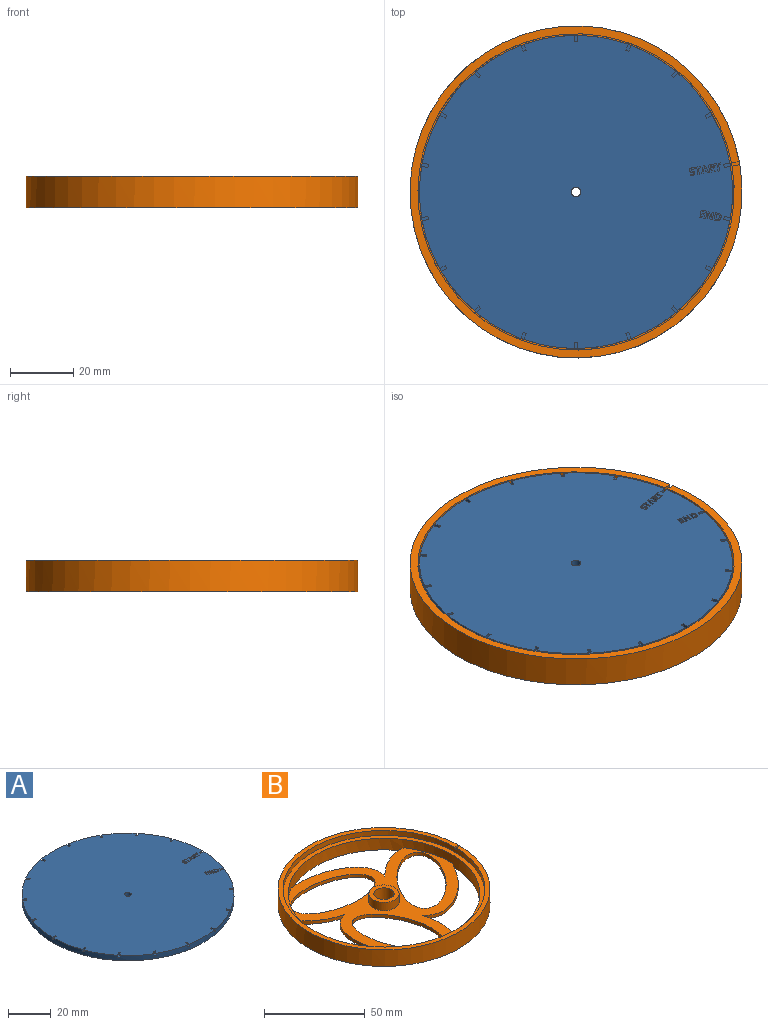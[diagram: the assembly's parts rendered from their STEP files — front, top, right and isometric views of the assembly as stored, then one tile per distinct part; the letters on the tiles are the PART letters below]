
ASSEMBLY  parts=2 mates=1
PART A: 206 faces, bbox 99x99x9 mm
  f0: plane 99x99mm, normal (0,0,1), area 7633.2mm2, adj f1,f9,f10,f11,f13,f14,f15,f17
  f1: cylinder r=49.5mm len=99mm, axis (0,0,1), area 915.1mm2, adj f0,f8,f9,f10,f12,f13,f14,f16
  f2: cylinder r=4.9mm len=9.8mm, axis (0,0,1), area 184.7mm2, adj f3,f5
  f3: plane 9.8x9.8mm, normal (0,0,-1), area 68.4mm2, adj f2,f205
  f4: cylinder r=7.5mm len=15mm, axis (0,0,1), area 47.1mm2, adj f5,f6
  f5: plane 15x15mm, normal (0,0,-1), area 101.3mm2, adj f2,f4
  f6: plane 95x95mm, normal (0,0,-1), area 6911.5mm2, adj f4,f7
  f7: cylinder r=47.5mm len=95mm, axis (0,0,1), area 298.5mm2, adj f6,f8
  f8: plane 99x99mm, normal (0,0,-1), area 609.5mm2, adj f1,f7
  f9: plane 1.88x1mm, normal (0.34,0.94,0), area 2mm2, adj f0,f1,f11,f12
  f10: plane 1.88x1mm, normal (-0.34,-0.94,0), area 2mm2, adj f0,f1,f11,f12
  f11: cylinder r=47.5mm len=1mm, axis (0,0,1), area 1mm2, adj f0,f9,f10,f12
  f12: plane 2.22x1.62mm, normal (0,0,1), area 2mm2, adj f1,f9,f10,f11
  f13: plane 1.53x1.29mm, normal (0.64,0.77,0), area 2mm2, adj f0,f1,f15,f16
  f14: plane 1.53x1.29mm, normal (-0.64,-0.77,0), area 2mm2, adj f0,f1,f15,f16
  f15: cylinder r=47.5mm len=1mm, axis (0,0,1), area 1mm2, adj f0,f13,f14,f16
  f16: plane 2.18x2.05mm, normal (0,0,1), area 2mm2, adj f1,f13,f14,f15
  f17: plane 1.73x1mm, normal (0.87,0.5,0), area 2mm2, adj f0,f1,f19,f20
  f18: plane 1.73x1mm, normal (-0.87,-0.5,0), area 2mm2, adj f0,f1,f19,f20
  f19: cylinder r=47.5mm len=1mm, axis (0,0,1), area 1mm2, adj f0,f17,f18,f20
  f20: plane 2.23x1.87mm, normal (0,0,1), area 2mm2, adj f1,f17,f18,f19
  f21: plane 1.97x1mm, normal (0.98,0.17,0), area 2mm2, adj f0,f1,f23,f24
  f22: plane 1.97x1mm, normal (-0.98,-0.17,0), area 2mm2, adj f0,f1,f23,f24
  f23: cylinder r=47.5mm len=1mm, axis (0,0,1), area 1mm2, adj f0,f21,f22,f24
  f24: plane 2.14x1.33mm, normal (0,0,1), area 2mm2, adj f1,f21,f22,f23
  f25: plane 1.97x1mm, normal (0.98,-0.17,0), area 2mm2, adj f0,f1,f27,f28
  f26: plane 1.97x1mm, normal (-0.98,0.17,0), area 2mm2, adj f0,f1,f27,f28
  f27: cylinder r=47.5mm len=1mm, axis (0,0,1), area 1mm2, adj f0,f25,f26,f28
  f28: plane 2.14x1.33mm, normal (0,0,1), area 2mm2, adj f1,f25,f26,f27
  f29: plane 1.73x1mm, normal (0.87,-0.5,0), area 2mm2, adj f0,f1,f31,f32
  f30: plane 1.73x1mm, normal (-0.87,0.5,0), area 2mm2, adj f0,f1,f31,f32
  f31: cylinder r=47.5mm len=1mm, axis (0,0,1), area 1mm2, adj f0,f29,f30,f32
  f32: plane 2.23x1.87mm, normal (0,0,1), area 2mm2, adj f1,f29,f30,f31
  f33: plane 1.53x1.29mm, normal (0.64,-0.77,0), area 2mm2, adj f0,f1,f35,f36
  f34: plane 1.53x1.29mm, normal (-0.64,0.77,0), area 2mm2, adj f0,f1,f35,f36
  f35: cylinder r=47.5mm len=1mm, axis (0,0,1), area 1mm2, adj f0,f33,f34,f36
  f36: plane 2.18x2.05mm, normal (0,0,1), area 2mm2, adj f1,f33,f34,f35
  f37: plane 1.88x1mm, normal (0.34,-0.94,0), area 2mm2, adj f0,f1,f39,f40
  f38: plane 1.88x1mm, normal (-0.34,0.94,0), area 2mm2, adj f0,f1,f39,f40
  f39: cylinder r=47.5mm len=1mm, axis (0,0,1), area 1mm2, adj f0,f37,f38,f40
  f40: plane 2.22x1.62mm, normal (0,0,1), area 2mm2, adj f1,f37,f38,f39
  f41: plane 2x1mm, normal (0,-1,0), area 2mm2, adj f0,f1,f43,f44
  f42: plane 2x1mm, normal (0,1,0), area 2mm2, adj f0,f1,f43,f44
  f43: cylinder r=47.5mm len=1mm, axis (0,0,1), area 1mm2, adj f0,f41,f42,f44
  f44: plane 2x1mm, normal (0,0,1), area 2mm2, adj f1,f41,f42,f43
  f45: plane 1.88x1mm, normal (-0.34,-0.94,0), area 2mm2, adj f0,f1,f47,f48
  f46: plane 1.88x1mm, normal (0.34,0.94,0), area 2mm2, adj f0,f1,f47,f48
  f47: cylinder r=47.5mm len=1mm, axis (0,0,1), area 1mm2, adj f0,f45,f46,f48
  f48: plane 2.22x1.62mm, normal (0,0,1), area 2mm2, adj f1,f45,f46,f47
  f49: plane 1.53x1.29mm, normal (-0.64,-0.77,0), area 2mm2, adj f0,f1,f51,f52
  f50: plane 1.53x1.29mm, normal (0.64,0.77,0), area 2mm2, adj f0,f1,f51,f52
  f51: cylinder r=47.5mm len=1mm, axis (0,0,1), area 1mm2, adj f0,f49,f50,f52
  f52: plane 2.18x2.05mm, normal (0,0,1), area 2mm2, adj f1,f49,f50,f51
  f53: plane 1.73x1mm, normal (-0.87,-0.5,0), area 2mm2, adj f0,f1,f55,f56
  f54: plane 1.73x1mm, normal (0.87,0.5,0), area 2mm2, adj f0,f1,f55,f56
  f55: cylinder r=47.5mm len=1mm, axis (0,0,1), area 1mm2, adj f0,f53,f54,f56
  f56: plane 2.23x1.87mm, normal (0,0,1), area 2mm2, adj f1,f53,f54,f55
  f57: plane 1.97x1mm, normal (-0.98,-0.17,0), area 2mm2, adj f0,f1,f59,f60
  f58: plane 1.97x1mm, normal (0.98,0.17,0), area 2mm2, adj f0,f1,f59,f60
  f59: cylinder r=47.5mm len=1mm, axis (0,0,1), area 1mm2, adj f0,f57,f58,f60
  f60: plane 2.14x1.33mm, normal (0,0,1), area 2mm2, adj f1,f57,f58,f59
  f61: plane 1.97x1mm, normal (-0.98,0.17,0), area 2mm2, adj f0,f1,f63,f64
  f62: plane 1.97x1mm, normal (0.98,-0.17,0), area 2mm2, adj f0,f1,f63,f64
  f63: cylinder r=47.5mm len=1mm, axis (0,0,1), area 1mm2, adj f0,f61,f62,f64
  f64: plane 2.14x1.33mm, normal (0,0,1), area 2mm2, adj f1,f61,f62,f63
  f65: plane 1.73x1mm, normal (-0.87,0.5,0), area 2mm2, adj f0,f1,f67,f68
  f66: plane 1.73x1mm, normal (0.87,-0.5,0), area 2mm2, adj f0,f1,f67,f68
  f67: cylinder r=47.5mm len=1mm, axis (0,0,1), area 1mm2, adj f0,f65,f66,f68
  f68: plane 2.23x1.87mm, normal (0,0,1), area 2mm2, adj f1,f65,f66,f67
  f69: plane 1.53x1.29mm, normal (-0.64,0.77,0), area 2mm2, adj f0,f1,f71,f72
  f70: plane 1.53x1.29mm, normal (0.64,-0.77,0), area 2mm2, adj f0,f1,f71,f72
  f71: cylinder r=47.5mm len=1mm, axis (0,0,1), area 1mm2, adj f0,f69,f70,f72
  f72: plane 2.18x2.05mm, normal (0,0,1), area 2mm2, adj f1,f69,f70,f71
  f73: plane 1.88x1mm, normal (-0.34,0.94,0), area 2mm2, adj f0,f1,f75,f76
  f74: plane 1.88x1mm, normal (0.34,-0.94,0), area 2mm2, adj f0,f1,f75,f76
  f75: cylinder r=47.5mm len=1mm, axis (0,0,1), area 1mm2, adj f0,f73,f74,f76
  f76: plane 2.22x1.62mm, normal (0,0,1), area 2mm2, adj f1,f73,f74,f75
  f77: plane 2x1mm, normal (0,-1,0), area 2mm2, adj f0,f1,f78,f80
  f78: cylinder r=47.5mm len=1mm, axis (0,0,1), area 1mm2, adj f0,f77,f79,f80
  f79: plane 2x1mm, normal (0,1,0), area 2mm2, adj f0,f1,f78,f80
  f80: plane 2x1mm, normal (0,0,1), area 2mm2, adj f1,f77,f78,f79
  f81: extruded ~0.7x0.39mm, area 0.3mm2, adj f0,f82,f108,f109
  f82: extruded ~0.7x0.46mm, area 0.4mm2, adj f0,f81,f83,f109
  f83: extruded ~0.7x0.32mm, area 0.3mm2, adj f0,f82,f84,f109
  f84: extruded ~0.7x0.1mm, area 0.1mm2, adj f0,f83,f85,f109
  f85: extruded ~0.7x0.12mm, area 0.1mm2, adj f0,f84,f86,f109
  f86: extruded ~0.7x0.17mm, area 0.1mm2, adj f0,f85,f87,f109
  f87: extruded ~0.7x0.22mm, area 0.2mm2, adj f0,f86,f88,f109
  f88: extruded ~0.7x0.25mm, area 0.2mm2, adj f0,f87,f89,f109
  f89: extruded ~0.7x0.32mm, area 0.2mm2, adj f0,f88,f90,f109
  f90: plane 0.7x0.39mm, normal (-0.92,0.38,0), area 0.3mm2, adj f0,f89,f91,f109
  f91: extruded ~0.7x0.35mm, area 0.3mm2, adj f0,f90,f92,f109
  f92: extruded ~0.7x0.36mm, area 0.3mm2, adj f0,f91,f93,f109
  f93: extruded ~0.7x0.59mm, area 0.4mm2, adj f0,f92,f94,f109
  f94: extruded ~0.7x0.5mm, area 0.4mm2, adj f0,f93,f95,f109
  f95: extruded ~0.7x0.29mm, area 0.2mm2, adj f0,f94,f96,f109
  f96: extruded ~0.7x0.22mm, area 0.2mm2, adj f0,f95,f97,f109
  f97: extruded ~0.7x0.33mm, area 0.3mm2, adj f0,f96,f98,f109
  f98: extruded ~0.7x0.31mm, area 0.2mm2, adj f0,f97,f99,f109
  f99: extruded ~0.7x0.12mm, area 0.1mm2, adj f0,f98,f100,f109
  f100: extruded ~0.7x0.13mm, area 0.1mm2, adj f0,f99,f101,f109
  f101: extruded ~0.7x0.19mm, area 0.2mm2, adj f0,f100,f102,f109
  f102: extruded ~0.7x0.26mm, area 0.2mm2, adj f0,f101,f103,f109
  f103: extruded ~0.7x0.31mm, area 0.2mm2, adj f0,f102,f104,f109
  f104: extruded ~0.7x0.41mm, area 0.3mm2, adj f0,f103,f105,f109
  f105: plane 0.7x0.47mm, normal (1,0,0), area 0.3mm2, adj f0,f104,f106,f109
  f106: extruded ~0.7x0.68mm, area 0.5mm2, adj f0,f105,f107,f109
  f107: extruded ~0.7x0.65mm, area 0.5mm2, adj f0,f106,f108,f109
  f108: extruded ~0.7x0.51mm, area 0.4mm2, adj f0,f81,f107,f109
  f109: plane 2.46x1.56mm, normal (0,0,1), area 2.2mm2, adj f81,f82,f83,f84,f85,f86,f87,f88
  f110: extruded ~0.92x0.7mm, area 0.7mm2, adj f0,f111,f121,f122
  f111: extruded ~0.75x0.7mm, area 0.7mm2, adj f0,f110,f112,f122
  f112: plane 0.71x0.7mm, normal (-0.34,-0.94,0), area 0.5mm2, adj f0,f111,f113,f122
  f113: plane 2.25x0.82mm, normal (0.94,-0.34,0), area 1.7mm2, adj f0,f112,f114,f122
  f114: plane 0.7x0.64mm, normal (0.34,0.94,0), area 0.5mm2, adj f0,f113,f115,f122
  f115: extruded ~1.02x0.7mm, area 0.7mm2, adj f0,f114,f121,f122
  f116: extruded ~0.96x0.7mm, area 0.9mm2, adj f117,f120,f122,f123
  f117: plane 0.7x0.2mm, normal (-0.34,-0.94,0), area 0.2mm2, adj f116,f118,f122,f123
  f118: plane 1.46x0.7mm, normal (-0.94,0.34,0), area 1.1mm2, adj f117,f119,f122,f123
  f119: plane 0.7x0.25mm, normal (0.34,0.94,0), area 0.2mm2, adj f118,f120,f122,f123
  f120: extruded ~0.96x0.7mm, area 0.8mm2, adj f116,f119,f122,f123
  f121: extruded ~0.73x0.7mm, area 0.7mm2, adj f0,f110,f115,f122
  f122: plane 2.64x2.41mm, normal (0,0,1), area 2.9mm2, adj f110,f111,f112,f113,f114,f115,f116,f117
  f123: plane 1.7x1.33mm, normal (0,0,1), area 1.3mm2, adj f116,f117,f118,f119,f120
  f124: plane 0.7x0.65mm, normal (-1,0,0), area 0.5mm2, adj f125,f142,f143,f204
  f125: plane 0.7x0.15mm, normal (0,1,0), area 0.1mm2, adj f124,f126,f143,f204
  f126: extruded ~0.7x0.36mm, area 0.3mm2, adj f125,f127,f143,f204
  f127: extruded ~0.7x0.24mm, area 0.2mm2, adj f126,f128,f143,f204
  f128: extruded ~0.7x0.25mm, area 0.2mm2, adj f127,f129,f143,f204
  f129: extruded ~0.7x0.36mm, area 0.3mm2, adj f128,f142,f143,f204
  f130: plane 0.7x0.27mm, normal (0,1,0), area 0.2mm2, adj f0,f131,f141,f143
  f131: plane 0.92x0.7mm, normal (0.85,0.53,0), area 0.8mm2, adj f0,f130,f132,f143
  f132: plane 0.7x0.56mm, normal (0,1,0), area 0.4mm2, adj f0,f131,f133,f143
  f133: extruded ~1.04x0.7mm, area 0.9mm2, adj f0,f132,f134,f143
  f134: extruded ~0.7x0.33mm, area 0.3mm2, adj f0,f133,f135,f143
  f135: extruded ~0.7x0.38mm, area 0.3mm2, adj f0,f134,f136,f143
  f136: extruded ~0.7x0.54mm, area 0.4mm2, adj f0,f135,f137,f143
  f137: extruded ~0.72x0.7mm, area 0.5mm2, adj f0,f136,f138,f143
  f138: plane 0.7x0.7mm, normal (0,-1,0), area 0.5mm2, adj f0,f137,f139,f143
  f139: plane 2.39x0.7mm, normal (1,0,0), area 1.7mm2, adj f0,f138,f140,f143
  f140: plane 0.7x0.51mm, normal (0,1,0), area 0.4mm2, adj f0,f139,f141,f143
  f141: plane 0.92x0.7mm, normal (-1,0,0), area 0.6mm2, adj f0,f130,f140,f143
  f142: plane 0.7x0.16mm, normal (0,-1,0), area 0.1mm2, adj f124,f129,f143,f204
  f143: plane 2.39x1.91mm, normal (0,0,1), area 2.8mm2, adj f124,f125,f126,f127,f128,f129,f130,f131
  f144: plane 0.7x0.55mm, normal (0,1,0), area 0.4mm2, adj f0,f145,f155,f156
  f145: plane 2.4x0.85mm, normal (-0.94,-0.33,0), area 1.8mm2, adj f0,f144,f146,f156
  f146: plane 0.7x0.62mm, normal (0,-1,0), area 0.4mm2, adj f0,f145,f147,f156
  f147: plane 2.4x0.84mm, normal (0.94,-0.33,0), area 1.8mm2, adj f0,f146,f148,f156
  f148: plane 0.7x0.55mm, normal (0,1,0), area 0.4mm2, adj f0,f147,f149,f156
  f149: plane 0.7x0.57mm, normal (-0.96,0.29,0), area 0.4mm2, adj f0,f148,f150,f156
  f150: plane 0.87x0.7mm, normal (0,1,0), area 0.6mm2, adj f0,f149,f155,f156
  f151: plane 0.7x0.62mm, normal (0,-1,0), area 0.4mm2, adj f152,f154,f156,f157
  f152: extruded ~1.03x0.7mm, area 0.8mm2, adj f151,f153,f156,f157
  f153: extruded ~0.7x0.16mm, area 0.1mm2, adj f152,f154,f156,f157
  f154: extruded ~0.87x0.7mm, area 0.6mm2, adj f151,f153,f156,f157
  f155: plane 0.7x0.57mm, normal (0.96,0.29,0), area 0.4mm2, adj f0,f144,f150,f156
  f156: plane 2.4x2.31mm, normal (0,0,1), area 2.6mm2, adj f144,f145,f146,f147,f148,f149,f150,f151
  f157: plane 1.03x0.62mm, normal (0,0,1), area 0.3mm2, adj f151,f152,f153,f154
  f158: plane 0.7x0.39mm, normal (-0.94,0.34,0), area 0.3mm2, adj f0,f159,f169,f170
  f159: plane 0.82x0.7mm, normal (-0.34,-0.94,0), area 0.6mm2, adj f0,f158,f160,f170
  f160: plane 0.7x0.58mm, normal (-0.94,0.34,0), area 0.4mm2, adj f0,f159,f161,f170
  f161: plane 0.76x0.7mm, normal (0.34,0.94,0), area 0.6mm2, adj f0,f160,f162,f170
  f162: plane 0.7x0.39mm, normal (-0.94,0.34,0), area 0.3mm2, adj f0,f161,f163,f170
  f163: plane 0.76x0.7mm, normal (-0.34,-0.94,0), area 0.6mm2, adj f0,f162,f164,f170
  f164: plane 0.7x0.49mm, normal (-0.94,0.34,0), area 0.4mm2, adj f0,f163,f165,f170
  f165: plane 0.82x0.7mm, normal (0.34,0.94,0), area 0.6mm2, adj f0,f164,f166,f170
  f166: plane 0.7x0.39mm, normal (-0.94,0.34,0), area 0.3mm2, adj f0,f165,f167,f170
  f167: plane 1.29x0.7mm, normal (-0.34,-0.94,0), area 1mm2, adj f0,f166,f168,f170
  f168: plane 2.25x0.82mm, normal (0.94,-0.34,0), area 1.7mm2, adj f0,f167,f169,f170
  f169: plane 1.29x0.7mm, normal (0.34,0.94,0), area 1mm2, adj f0,f158,f168,f170
  f170: plane 2.72x2.11mm, normal (0,0,1), area 2.3mm2, adj f158,f159,f160,f161,f162,f163,f164,f165
  f171: plane 2.25x0.82mm, normal (-0.94,0.34,0), area 1.7mm2, adj f0,f172,f184,f185
  f172: plane 0.7x0.43mm, normal (-0.34,-0.94,0), area 0.3mm2, adj f0,f171,f173,f185
  f173: plane 1.06x0.7mm, normal (0.94,-0.34,0), area 0.8mm2, adj f0,f172,f174,f185
  f174: extruded ~0.7x0.63mm, area 0.5mm2, adj f0,f173,f175,f185
  f175: plane 0.7x0.01mm, normal (-0.34,-0.94,0), area 0mm2, adj f0,f174,f176,f185
  f176: plane 2.04x0.7mm, normal (-0.98,-0.18,0), area 1.4mm2, adj f0,f175,f177,f185
  f177: plane 0.7x0.6mm, normal (-0.34,-0.94,0), area 0.4mm2, adj f0,f176,f178,f185
  f178: plane 2.25x0.82mm, normal (0.94,-0.34,0), area 1.7mm2, adj f0,f177,f179,f185
  f179: plane 0.7x0.43mm, normal (0.34,0.94,0), area 0.3mm2, adj f0,f178,f180,f185
  f180: plane 1.06x0.7mm, normal (-0.94,0.34,0), area 0.8mm2, adj f0,f179,f181,f185
  f181: extruded ~0.7x0.65mm, area 0.5mm2, adj f0,f180,f182,f185
  f182: plane 0.7x0.01mm, normal (0.34,0.94,0), area 0mm2, adj f0,f181,f183,f185
  f183: plane 2.05x0.7mm, normal (0.99,0.17,0), area 1.5mm2, adj f0,f182,f184,f185
  f184: plane 0.7x0.61mm, normal (0.34,0.94,0), area 0.5mm2, adj f0,f171,f183,f185
  f185: plane 2.97x2.81mm, normal (0,0,1), area 3.2mm2, adj f171,f172,f173,f174,f175,f176,f177,f178
  f186: plane 1.97x0.7mm, normal (-1,0,0), area 1.4mm2, adj f0,f187,f193,f194
  f187: plane 0.7x0.65mm, normal (0,1,0), area 0.5mm2, adj f0,f186,f188,f194
  f188: plane 0.7x0.42mm, normal (-1,0,0), area 0.3mm2, adj f0,f187,f189,f194
  f189: plane 1.8x0.7mm, normal (0,-1,0), area 1.3mm2, adj f0,f188,f190,f194
  f190: plane 0.7x0.42mm, normal (1,0,0), area 0.3mm2, adj f0,f189,f191,f194
  f191: plane 0.7x0.65mm, normal (0,1,0), area 0.5mm2, adj f0,f190,f192,f194
  f192: plane 1.97x0.7mm, normal (1,0,0), area 1.4mm2, adj f0,f191,f193,f194
  f193: plane 0.7x0.51mm, normal (0,1,0), area 0.4mm2, adj f0,f186,f192,f194
  f194: plane 2.39x1.8mm, normal (0,0,1), area 1.8mm2, adj f186,f187,f188,f189,f190,f191,f192,f193
  f195: plane 1.97x0.7mm, normal (-1,0,0), area 1.4mm2, adj f0,f196,f202,f203
  f196: plane 0.7x0.65mm, normal (0,1,0), area 0.5mm2, adj f0,f195,f197,f203
  f197: plane 0.7x0.42mm, normal (-1,0,0), area 0.3mm2, adj f0,f196,f198,f203
  f198: plane 1.8x0.7mm, normal (0,-1,0), area 1.3mm2, adj f0,f197,f199,f203
  f199: plane 0.7x0.42mm, normal (1,0,0), area 0.3mm2, adj f0,f198,f200,f203
  f200: plane 0.7x0.65mm, normal (0,1,0), area 0.5mm2, adj f0,f199,f201,f203
  f201: plane 1.97x0.7mm, normal (1,0,0), area 1.4mm2, adj f0,f200,f202,f203
  f202: plane 0.7x0.51mm, normal (0,1,0), area 0.4mm2, adj f0,f195,f201,f203
  f203: plane 2.39x1.8mm, normal (0,0,1), area 1.8mm2, adj f195,f196,f197,f198,f199,f200,f201,f202
  f204: plane 0.65x0.63mm, normal (0,0,1), area 0.4mm2, adj f124,f125,f126,f127,f128,f129,f142
  f205: cylinder r=1.5mm len=9mm, axis (0,0,1), area 84.8mm2, adj f0,f3
PART B: 22 faces, bbox 105x105x10 mm
  f0: cylinder r=50mm len=100mm, axis (0,0,-1), area 941.5mm2, adj f1,f17,f19,f20,f21
  f1: plane 105x105mm, normal (0,0,1), area 802.5mm2, adj f0,f18,f19,f20
  f2: extruded ~20.9x15.53mm, area 54mm2, adj f3,f11,f12,f16
  f3: extruded ~47.36x11.77mm, area 109.6mm2, adj f2,f11,f12,f16
  f4: extruded ~25.87x4.51mm, area 54mm2, adj f5,f11,f12,f16
  f5: extruded ~42.12x26.27mm, area 109.6mm2, adj f4,f11,f12,f16
  f6: extruded ~23.9x10.61mm, area 54mm2, adj f7,f11,f12,f16
  f7: extruded ~40.65x25.84mm, area 109.6mm2, adj f6,f11,f12,f16
  f8: extruded ~46.07x28.02mm, area 233.7mm2, adj f11,f12
  f9: extruded ~47.55x25.08mm, area 233.7mm2, adj f11,f12
  f10: extruded ~40.12x36mm, area 233.7mm2, adj f11,f12
  f11: plane 89.81x88.81mm, normal (0,0,1), area 2115.9mm2, adj f2,f3,f4,f5,f6,f7,f8,f9
  f12: plane 105x105mm, normal (0,0,-1), area 3784.8mm2, adj f2,f3,f4,f5,f6,f7,f8,f9
  f13: cylinder r=7.5mm len=15mm, axis (0,0,-1), area 235.6mm2, adj f11,f15
  f14: cylinder r=5mm len=10mm, axis (0,0,-1), area 219.9mm2, adj f12,f15
  f15: plane 15x15mm, normal (0,0,1), area 98.2mm2, adj f13,f14
  f16: cylinder r=47.5mm len=95mm, axis (0,0,-1), area 1926.8mm2, adj f2,f3,f4,f5,f6,f7,f11,f12
  f17: plane 100x100mm, normal (0,0,1), area 765.8mm2, adj f0,f16
  f18: cylinder r=52.5mm len=105mm, axis (0,0,-1), area 3297.7mm2, adj f1,f12,f19,f20,f21
  f19: plane 2.5x1mm, normal (0,-1,0), area 2.5mm2, adj f0,f1,f18,f21
  f20: plane 2.5x1mm, normal (0,1,0), area 2.5mm2, adj f0,f1,f18,f21
  f21: plane 2.5x1mm, normal (0,0,1), area 2.5mm2, adj f0,f18,f19,f20
PLACE A rot(axis=(0,0,1),10deg) t=(-9.05,-1.37,0)mm
PLACE B rot(axis=(0,0,1),10deg) t=(-9.05,-1.37,-3)mm fixed
MATE revolute B.f0 <-> A.f1  axis (0,0,1) through (-9.05,-1.37,4)mm
